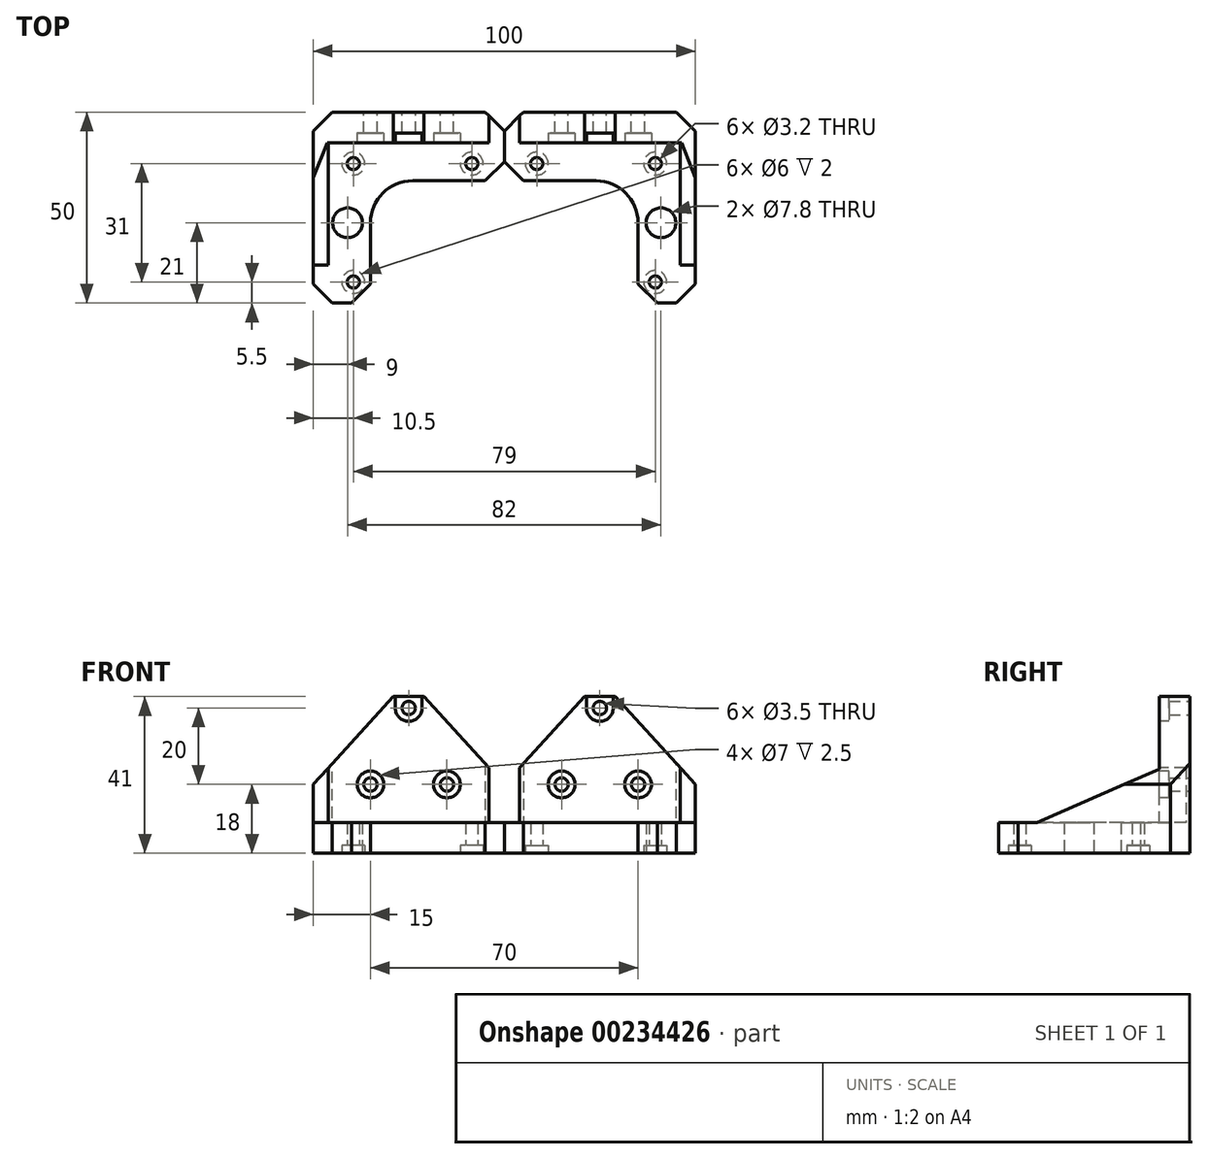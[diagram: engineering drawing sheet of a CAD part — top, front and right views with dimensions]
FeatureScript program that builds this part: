
annotation { "Feature Type Name" : "Feature", "Feature Type Description" : "" }
export const myFeature = defineFeature(function(context is Context, id is Id, definition is map)
    precondition{}
    {
        {
            var Q0;
            Q0=qCreatedBy(makeId("Top.planeOp"),FACE);
            var sketch = newSketch(context, id + "F0", { "sketchPlane" : qUnion([Q0])});
            skLineSegment(sketch, "E0", {"start": v(0, 0) * mm, "end": v(-50, 0) * mm});
            skLineSegment(sketch, "E1", {"start": v(-50, 0) * mm, "end": v(-50, -50) * mm});
            skCircle(sketch, "E2", {"center": v(-41, -29) * mm, "radius": 3.9 * mm});
            skLineSegment(sketch, "E3", {"start": v(0, -18) * mm, "end": v(0, 0) * mm});
            skCircle(sketch, "E4", {"center": v(-39.5, -13.5) * mm, "radius": 1.6 * mm});
            skCircle(sketch, "E5", {"center": v(-8.5, -13.5) * mm, "radius": 1.6 * mm});
            skCircle(sketch, "E6", {"center": v(-39.5, -44.5) * mm, "radius": 1.6 * mm});
            skLineSegment(sketch, "E7", {"start": v(-35, -50) * mm, "end": v(-50, -50) * mm});
            skLineSegment(sketch, "E8", {"start": v(-50, -8) * mm, "end": v(0, -8) * mm});
            skArc(sketch, "E9", {"start": v(-24, -18) * mm, "mid": v(-31.78, -21.22) * mm, "end": v(-35, -29) * mm});
            skLineSegment(sketch, "E10", {"start": v(0, -18) * mm, "end": v(-24, -18) * mm});
            skLineSegment(sketch, "E11", {"start": v(-35, -50) * mm, "end": v(-35, -29) * mm});
            skCircle(sketch, "E12", {"center": v(-39.5, -44.5) * mm, "radius": 3 * mm});
            skCircle(sketch, "E13", {"center": v(-8.5, -13.5) * mm, "radius": 3 * mm});
            skCircle(sketch, "E14", {"center": v(-39.5, -13.5) * mm, "radius": 3 * mm});
            skSolve(sketch);
        }
        {
            var Q0;
            {var subQ0=sQuery(id+"F0.wireOp",EDGE,"E0");Q0=makeQuery(id+"F0.imprint","IMPRINT",FACE,{"disambiguationData":[TD([[makeQuery(id+"F0.imprint","IMPRINT",EDGE,{"derivedFrom":subQ0}),1.0]])]});}
            var Q1;
            Q1=makeQuery(id+"F0.imprint","IMPRINT",FACE,{"disambiguationData":[TD([[makeQuery(id+"F0.imprint","IMPRINT",EDGE,{"derivedFrom":sQuery(id+"F0.wireOp",EDGE,"E6")}),-1.0]])]});
            var Q2;
            Q2=makeQuery(id+"F0.imprint","IMPRINT",FACE,{"disambiguationData":[TD([[makeQuery(id+"F0.imprint","IMPRINT",EDGE,{"derivedFrom":sQuery(id+"F0.wireOp",EDGE,"E5")}),-1.0]])]});
            var Q3;
            Q3=makeQuery(id+"F0.imprint","IMPRINT",FACE,{"disambiguationData":[TD([[makeQuery(id+"F0.imprint","IMPRINT",EDGE,{"derivedFrom":sQuery(id+"F0.wireOp",EDGE,"E4")}),-1.0]])]});
            var Q4;
            Q4=makeQuery(id+"F0.imprint","IMPRINT",FACE,{"disambiguationData":[TD([[makeQuery(id+"F0.imprint","IMPRINT",EDGE,{"derivedFrom":sQuery(id+"F0.wireOp",EDGE,"E2")}),-1.0]])]});
            extrude(context, id + "F1", {"entities" : qUnion([Q0, Q1, Q2, Q3, Q4]), "depth" : 8 * mm});
        }
        {
            var Q0;
            {var subQ0=sQuery(id+"F0.wireOp",EDGE,"E0");Q0=makeQuery(id+"F0.imprint","IMPRINT",FACE,{"disambiguationData":[TD([[makeQuery(id+"F0.imprint","IMPRINT",EDGE,{"derivedFrom":subQ0}),1.0]])]});}
            extrude(context, id + "F2", {"entities" : qUnion([Q0]), "operationType" : NewBodyOperationType.ADD, "depth" : 41 * mm});
        }
        {
            var Q0;
            {var subQ0=sQuery(id+"F0.wireOp",EDGE,"E0");Q0=makeQuery(id+"F2.boolean.opBoolean","MERGE",FACE,{"derivedFrom":[makeQuery(id+"F1.opExtrude","SWEPT_FACE",FACE,{"disambiguationData":[OSD([subQ0])]}),makeQuery(id+"F2.opExtrude","SWEPT_FACE",FACE,{"disambiguationData":[OSD([subQ0])]})]});}
            var sketch = newSketch(context, id + "F3", { "sketchPlane" : qUnion([Q0])});
            skCircle(sketch, "E15", {"center": v(15, 18) * mm, "radius": 1.75 * mm});
            skCircle(sketch, "E16", {"center": v(35, 18) * mm, "radius": 1.75 * mm});
            skCircle(sketch, "E17", {"center": v(25, 38) * mm, "radius": 1.75 * mm});
            skLineSegment(sketch, "E18", {"start": v(25, 41) * mm, "end": v(29, 41) * mm});
            skLineSegment(sketch, "E19", {"start": v(29, 41) * mm, "end": v(21, 41) * mm});
            skLineSegment(sketch, "E20", {"start": v(50, 18) * mm, "end": v(29, 41) * mm});
            skLineSegment(sketch, "E21", {"start": v(50, 18) * mm, "end": v(50, 41) * mm});
            skLineSegment(sketch, "E22", {"start": v(50, 41) * mm, "end": v(29, 41) * mm});
            skLineSegment(sketch, "E23", {"start": v(21, 41) * mm, "end": v(0, 18) * mm});
            skLineSegment(sketch, "E24", {"start": v(0, 18) * mm, "end": v(0, 41) * mm});
            skLineSegment(sketch, "E25", {"start": v(0, 41) * mm, "end": v(21, 41) * mm});
            skSolve(sketch);
        }
        {
            var Q0;
            {var subQ0=sQuery(id+"F0.wireOp",EDGE,"E1");Q0=makeQuery(id+"F2.boolean.opBoolean","MERGE",FACE,{"derivedFrom":[makeQuery(id+"F1.opExtrude","SWEPT_FACE",FACE,{"disambiguationData":[OSD([subQ0])]}),makeQuery(id+"F2.opExtrude","SWEPT_FACE",FACE,{"disambiguationData":[OSD([subQ0])]})]});}
            var sketch = newSketch(context, id + "F4", { "sketchPlane" : qUnion([Q0])});
            skLineSegment(sketch, "E26", {"start": v(40, 8) * mm, "end": v(8, 22) * mm});
            skLineSegment(sketch, "E27", {"start": v(40, 8) * mm, "end": v(40, 0) * mm});
            skLineSegment(sketch, "E28", {"start": v(40, 0) * mm, "end": v(0, 0) * mm});
            skLineSegment(sketch, "E29", {"start": v(0, 0) * mm, "end": v(0, 22) * mm});
            skLineSegment(sketch, "E30", {"start": v(0, 22) * mm, "end": v(8, 22) * mm});
            skSolve(sketch);
        }
        {
            var Q0;
            Q0 = qSketchRegion(id + "F4", true);
            extrude(context, id + "F5", {"entities" : qUnion([Q0]), "operationType" : NewBodyOperationType.ADD, "oppositeDirection" : true, "depth" : 4 * mm});
        }
        {
            var Q0;
            Q0=makeQuery(id+"F3.imprint","IMPRINT",FACE,{"disambiguationData":[TD([[makeQuery(id+"F3.imprint","IMPRINT",EDGE,{"derivedFrom":sQuery(id+"F3.wireOp",EDGE,"E23")}),-1.0]])]});
            var Q1;
            Q1=makeQuery(id+"F3.imprint","IMPRINT",FACE,{"disambiguationData":[TD([[makeQuery(id+"F3.imprint","IMPRINT",EDGE,{"derivedFrom":sQuery(id+"F3.wireOp",EDGE,"E20")}),-1.0]])]});
            var Q2;
            Q2=makeQuery(id+"F3.imprint","IMPRINT",FACE,{"disambiguationData":[TD([[makeQuery(id+"F3.imprint","IMPRINT",EDGE,{"derivedFrom":sQuery(id+"F3.wireOp",EDGE,"E17")}),1.0]])]});
            var Q3;
            Q3=makeQuery(id+"F3.imprint","IMPRINT",FACE,{"disambiguationData":[TD([[makeQuery(id+"F3.imprint","IMPRINT",EDGE,{"derivedFrom":sQuery(id+"F3.wireOp",EDGE,"E16")}),1.0]])]});
            var Q4;
            Q4=makeQuery(id+"F3.imprint","IMPRINT",FACE,{"disambiguationData":[TD([[makeQuery(id+"F3.imprint","IMPRINT",EDGE,{"derivedFrom":sQuery(id+"F3.wireOp",EDGE,"E15")}),1.0]])]});
            extrude(context, id + "F6", {"entities" : qUnion([Q0, Q1, Q2, Q3, Q4]), "operationType" : NewBodyOperationType.REMOVE, "oppositeDirection" : true, "depth" : 25 * mm});
        }
        {
            var Q0;
            Q0=makeQuery(id+"F2.opExtrude","SWEPT_FACE",FACE,{"disambiguationData":[OSD([sQuery(id+"F0.wireOp",EDGE,"E8")])]});
            var sketch = newSketch(context, id + "F7", { "sketchPlane" : qUnion([Q0])});
            skCircle(sketch, "E31", {"center": v(-35, 18) * mm, "radius": 3.5 * mm});
            skCircle(sketch, "E32", {"center": v(-15, 18) * mm, "radius": 3.5 * mm});
            skArc(sketch, "E33", {"start": v(-28.5, 38) * mm, "mid": v(-25, 34.5) * mm, "end": v(-21.5, 38) * mm});
            skLineSegment(sketch, "E34", {"start": v(-28.5, 38) * mm, "end": v(-28.5, 41) * mm});
            skLineSegment(sketch, "E35", {"start": v(-21.5, 38) * mm, "end": v(-21.5, 41) * mm});
            skLineSegment(sketch, "E36", {"start": v(-21.5, 41) * mm, "end": v(-28.5, 41) * mm});
            skLineSegment(sketch, "E37", {"start": v(-4, 8) * mm, "end": v(-4, 22.38) * mm});
            skLineSegment(sketch, "E38", {"start": v(-4, 22.38) * mm, "end": v(0, 18) * mm});
            skLineSegment(sketch, "E39", {"start": v(0, 18) * mm, "end": v(0, 8) * mm});
            skLineSegment(sketch, "E40", {"start": v(0, 8) * mm, "end": v(-4, 8) * mm});
            skSolve(sketch);
        }
        {
            var Q0;
            Q0=makeQuery(id+"F7.imprint","IMPRINT",FACE,{"disambiguationData":[TD([[makeQuery(id+"F7.imprint","IMPRINT",EDGE,{"derivedFrom":sQuery(id+"F7.wireOp",EDGE,"E31")}),1.0]])]});
            var Q1;
            Q1=makeQuery(id+"F7.imprint","IMPRINT",FACE,{"disambiguationData":[TD([[makeQuery(id+"F7.imprint","IMPRINT",EDGE,{"derivedFrom":sQuery(id+"F7.wireOp",EDGE,"E33")}),1.0]])]});
            var Q2;
            Q2=makeQuery(id+"F7.imprint","IMPRINT",FACE,{"disambiguationData":[TD([[makeQuery(id+"F7.imprint","IMPRINT",EDGE,{"derivedFrom":sQuery(id+"F7.wireOp",EDGE,"E32")}),1.0]])]});
            extrude(context, id + "F8", {"entities" : qUnion([Q0, Q1, Q2]), "operationType" : NewBodyOperationType.REMOVE, "oppositeDirection" : true, "depth" : 2.5 * mm});
        }
        {
            var Q0;
            Q0=makeQuery(id+"F7.imprint","IMPRINT",FACE,{"disambiguationData":[TD([[makeQuery(id+"F7.imprint","IMPRINT",EDGE,{"derivedFrom":sQuery(id+"F7.wireOp",EDGE,"E37")}),-1.0]])]});
            extrude(context, id + "F9", {"entities" : qUnion([Q0]), "operationType" : NewBodyOperationType.REMOVE, "oppositeDirection" : true, "depth" : 25 * mm});
        }
        {
            var Q0;
            Q0=makeQuery(id+"F1.opExtrude","SWEPT_EDGE",EDGE,{"disambiguationData":[OSD([sQuery(id+"F0.wireOp",EDGE,"E3"),sQuery(id+"F0.wireOp",EDGE,"E10")])]});
            var Q1;
            {var subQ0=sQuery(id+"F0.wireOp",EDGE,"E3");var subQ1=sQuery(id+"F0.wireOp",EDGE,"E0");Q1=makeQuery(id+"F2.boolean.opBoolean","MERGE",EDGE,{"derivedFrom":[makeQuery(id+"F1.opExtrude","SWEPT_EDGE",EDGE,{"disambiguationData":[OSD([subQ1,subQ0])]}),makeQuery(id+"F2.opExtrude","SWEPT_EDGE",EDGE,{"disambiguationData":[OSD([subQ1,subQ0])]})]});}
            var Q2;
            Q2=makeQuery(id+"F1.opExtrude","SWEPT_EDGE",EDGE,{"disambiguationData":[OSD([sQuery(id+"F0.wireOp",EDGE,"E7"),sQuery(id+"F0.wireOp",EDGE,"E11")])]});
            var Q3;
            Q3=makeQuery(id+"F1.opExtrude","SWEPT_EDGE",EDGE,{"disambiguationData":[OSD([sQuery(id+"F0.wireOp",EDGE,"E1"),sQuery(id+"F0.wireOp",EDGE,"E7")])]});
            var Q4;
            {var subQ0=sQuery(id+"F0.wireOp",EDGE,"E1");var subQ1=sQuery(id+"F0.wireOp",EDGE,"E0");Q4=makeQuery(id+"F2.boolean.opBoolean","MERGE",EDGE,{"derivedFrom":[makeQuery(id+"F1.opExtrude","SWEPT_EDGE",EDGE,{"disambiguationData":[OSD([subQ1,subQ0])]}),makeQuery(id+"F2.opExtrude","SWEPT_EDGE",EDGE,{"disambiguationData":[OSD([subQ1,subQ0])]})]});}
            chamfer(context, id + "F10", {"entities" : qUnion([Q0, Q1, Q2, Q3, Q4]), "width" : 5 * mm, "tangentPropagation" : true});
        }
        {
            var Q0;
            Q0=makeQuery(id+"F0.imprint","IMPRINT",FACE,{"disambiguationData":[TD([[makeQuery(id+"F0.imprint","IMPRINT",EDGE,{"derivedFrom":sQuery(id+"F0.wireOp",EDGE,"E6")}),-1.0]])]});
            var Q1;
            Q1=makeQuery(id+"F0.imprint","IMPRINT",FACE,{"disambiguationData":[TD([[makeQuery(id+"F0.imprint","IMPRINT",EDGE,{"derivedFrom":sQuery(id+"F0.wireOp",EDGE,"E5")}),-1.0]])]});
            var Q2;
            Q2=makeQuery(id+"F0.imprint","IMPRINT",FACE,{"disambiguationData":[TD([[makeQuery(id+"F0.imprint","IMPRINT",EDGE,{"derivedFrom":sQuery(id+"F0.wireOp",EDGE,"E4")}),-1.0]])]});
            extrude(context, id + "F11", {"entities" : qUnion([Q0, Q1, Q2]), "operationType" : NewBodyOperationType.REMOVE, "depth" : 2 * mm});
        }
        {
            var Q0;
            Q0=makeQuery(id+"F1.opExtrude","SWEPT_BODY",BODY,{"disambiguationData":[OSD([sQuery(id+"F0.wireOp",EDGE,"E0"),sQuery(id+"F0.wireOp",EDGE,"E1"),sQuery(id+"F0.wireOp",EDGE,"E2"),sQuery(id+"F0.wireOp",EDGE,"E3"),sQuery(id+"F0.wireOp",EDGE,"E4"),sQuery(id+"F0.wireOp",EDGE,"E5"),sQuery(id+"F0.wireOp",EDGE,"E6"),sQuery(id+"F0.wireOp",EDGE,"E7"),sQuery(id+"F0.wireOp",EDGE,"E9"),sQuery(id+"F0.wireOp",EDGE,"E10"),sQuery(id+"F0.wireOp",EDGE,"E11")])]});
            var Q1;
            {var subQ0=sQuery(id+"F0.wireOp",EDGE,"E3");Q1=makeQuery(id+"F2.boolean.opBoolean","MERGE",FACE,{"derivedFrom":[makeQuery(id+"F1.opExtrude","SWEPT_FACE",FACE,{"disambiguationData":[OSD([subQ0])]}),makeQuery(id+"F2.opExtrude","SWEPT_FACE",FACE,{"disambiguationData":[OSD([subQ0])]})]});}
            mirror(context, id + "F12", {"entities" : qUnion([Q0]), "mirrorPlane" : qUnion([Q1])});
        }
    });
